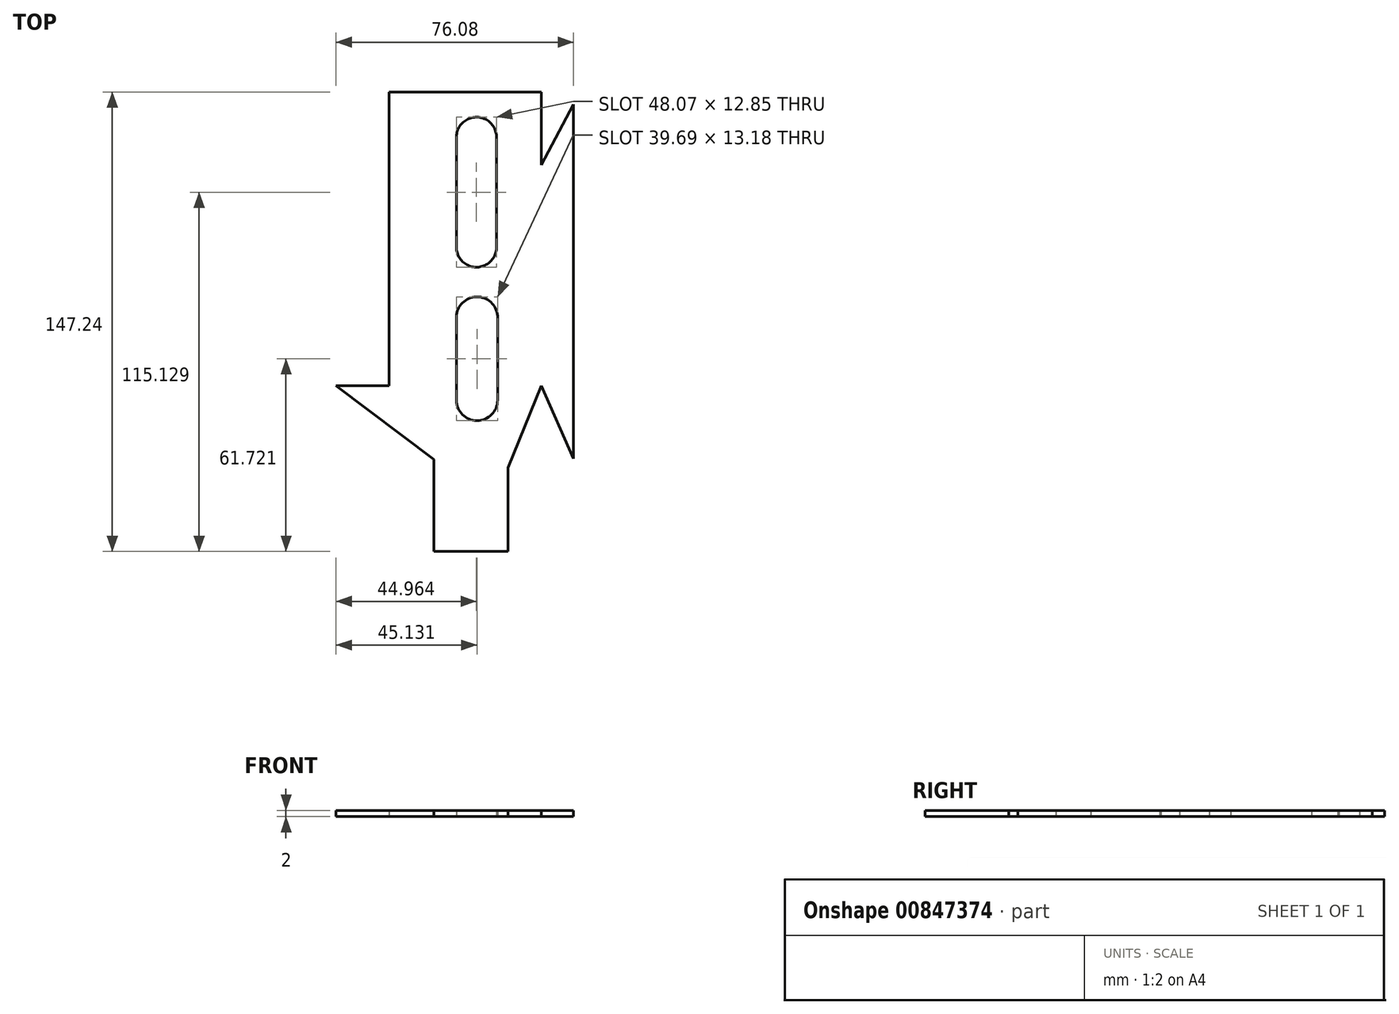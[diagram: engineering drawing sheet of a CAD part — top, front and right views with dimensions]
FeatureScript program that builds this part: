
annotation { "Feature Type Name" : "Feature", "Feature Type Description" : "" }
export const myFeature = defineFeature(function(context is Context, id is Id, definition is map)
    precondition{}
    {
        {
            var Q0;
            Q0=qCreatedBy(makeId("Top.planeOp"),FACE);
            var sketch = newSketch(context, id + "F0", { "sketchPlane" : qUnion([Q0])});
            skLineSegment(sketch, "E0.bottom", {"start": v(-52.45, 82.99) * mm, "end": v(47.55, 82.99) * mm});
            skLineSegment(sketch, "E0.top", {"start": v(-52.45, -67.01) * mm, "end": v(47.55, -67.01) * mm});
            skLineSegment(sketch, "E0.left", {"start": v(-52.45, 82.99) * mm, "end": v(-52.45, -67.01) * mm});
            skLineSegment(sketch, "E0.right", {"start": v(47.55, 82.99) * mm, "end": v(47.55, -67.01) * mm});
            skLineSegment(sketch, "E1", {"start": v(-7.17, -67.01) * mm, "end": v(-7.17, -37.57) * mm});
            skLineSegment(sketch, "E2", {"start": v(-7.17, -37.57) * mm, "end": v(-38.54, -13.87) * mm});
            skLineSegment(sketch, "E3", {"start": v(-38.54, -13.87) * mm, "end": v(-21.52, -13.87) * mm});
            skLineSegment(sketch, "E4", {"start": v(-21.52, -13.87) * mm, "end": v(-21.52, 80.23) * mm});
            skLineSegment(sketch, "E5", {"start": v(-21.52, 80.23) * mm, "end": v(27.2, 80.23) * mm});
            skLineSegment(sketch, "E6", {"start": v(27.2, 80.23) * mm, "end": v(27.2, 56.87) * mm});
            skLineSegment(sketch, "E7", {"start": v(27.2, 56.87) * mm, "end": v(37.54, 76.23) * mm});
            skLineSegment(sketch, "E8", {"start": v(37.54, 76.23) * mm, "end": v(37.54, -37.23) * mm});
            skLineSegment(sketch, "E9", {"start": v(37.54, -37.23) * mm, "end": v(27.2, -13.87) * mm});
            skLineSegment(sketch, "E10", {"start": v(27.2, -13.87) * mm, "end": v(16.52, -40.24) * mm});
            skLineSegment(sketch, "E11", {"start": v(16.52, -40.24) * mm, "end": v(16.52, -67.01) * mm});
            skLineSegment(sketch, "E12", {"start": v(16.52, -67.01) * mm, "end": v(-7.17, -67.01) * mm});
            skArc(sketch, "E13", {"start": v(12.85, 65.21) * mm, "mid": v(6.6, 72.16) * mm, "end": v(0, 65.55) * mm});
            skLineSegment(sketch, "E14", {"start": v(0, 65.55) * mm, "end": v(0, 30.84) * mm});
            skLineSegment(sketch, "E15", {"start": v(0, 30.84) * mm, "end": v(0, 65.55) * mm});
            skLineSegment(sketch, "E16", {"start": v(12.85, 65.21) * mm, "end": v(12.85, 30.5) * mm});
            skLineSegment(sketch, "E17", {"start": v(12.85, 30.5) * mm, "end": v(12.85, 65.21) * mm});
            skArc(sketch, "E18", {"start": v(0, 30.84) * mm, "mid": v(6.25, 24.08) * mm, "end": v(12.85, 30.5) * mm});
            skArc(sketch, "E19", {"start": v(13.18, 8.48) * mm, "mid": v(6.43, 14.56) * mm, "end": v(0, 8.15) * mm});
            skLineSegment(sketch, "E20", {"start": v(0, 8.15) * mm, "end": v(0, -18.55) * mm});
            skLineSegment(sketch, "E21", {"start": v(0, -18.55) * mm, "end": v(0, 8.15) * mm});
            skArc(sketch, "E22", {"start": v(0, -18.55) * mm, "mid": v(6.6, -25.14) * mm, "end": v(13.18, -18.55) * mm});
            skLineSegment(sketch, "E23", {"start": v(13.18, -18.55) * mm, "end": v(13.18, 8.48) * mm});
            skLineSegment(sketch, "E24", {"start": v(27.2, 56.87) * mm, "end": v(27.2, -13.87) * mm});
            skSolve(sketch);
        }
        {
            var Q0;
            Q0=makeQuery(id+"F0.imprint","IMPRINT",FACE,{"disambiguationData":[TD([[makeQuery(id+"F0.imprint","IMPRINT",EDGE,{"derivedFrom":sQuery(id+"F0.wireOp",EDGE,"E1")}),-1.0]])]});
            var Q1;
            Q1=makeQuery(id+"F0.imprint","IMPRINT",FACE,{"disambiguationData":[TD([[makeQuery(id+"F0.imprint","IMPRINT",EDGE,{"derivedFrom":sQuery(id+"F0.wireOp",EDGE,"E7")}),-1.0]])]});
            extrude(context, id + "F1", {"entities" : qUnion([Q0, Q1]), "depth" : 2 * mm, "offsetDistance" : 25 * mm});
        }
    });
